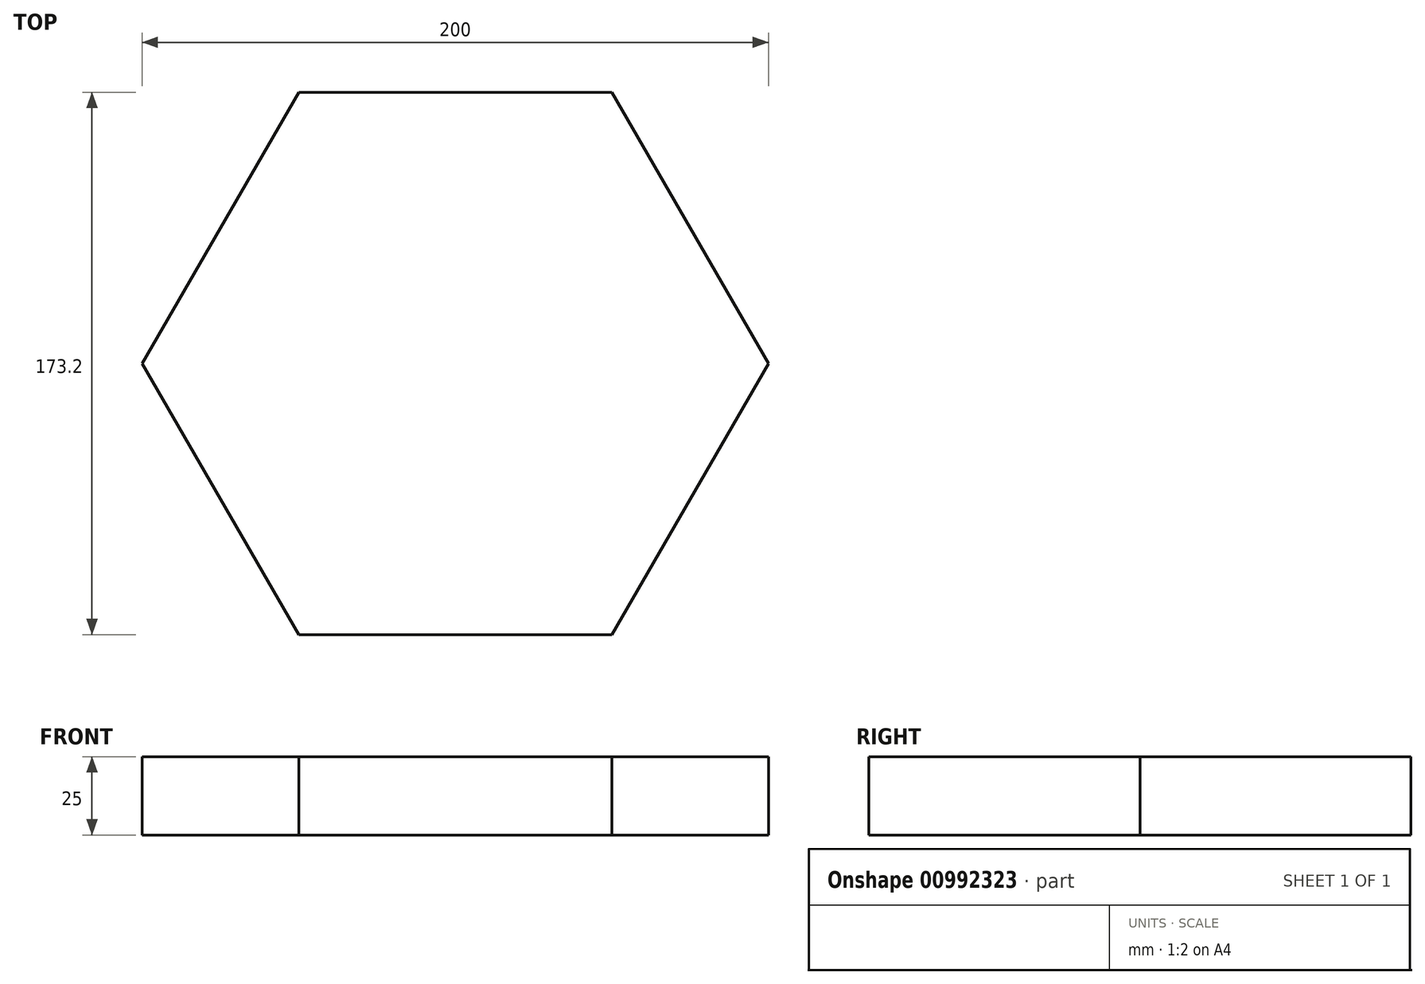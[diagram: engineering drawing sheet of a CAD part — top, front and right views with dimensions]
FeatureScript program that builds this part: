
annotation { "Feature Type Name" : "Feature", "Feature Type Description" : "" }
export const myFeature = defineFeature(function(context is Context, id is Id, definition is map)
    precondition{}
    {
        {
            var Q0;
            Q0=qCreatedBy(makeId("Top.planeOp"),FACE);
            var sketch = newSketch(context, id + "F0", { "sketchPlane" : qUnion([Q0])});
            skCircle(sketch, "E0", {"center": v(0, 0) * mm, "radius": 100 * mm});
            skLineSegment(sketch, "E1", {"start": v(0, 0) * mm, "end": v(100, 0) * mm, "construction": true});
            skLineSegment(sketch, "E2", {"start": v(0, 0) * mm, "end": v(50, 86.6) * mm, "construction": true});
            skLineSegment(sketch, "E3", {"start": v(0, 0) * mm, "end": v(-50, 86.6) * mm, "construction": true});
            skLineSegment(sketch, "E4", {"start": v(0, 0) * mm, "end": v(-100, 0) * mm, "construction": true});
            skLineSegment(sketch, "E5", {"start": v(0, 0) * mm, "end": v(-50, -86.6) * mm, "construction": true});
            skLineSegment(sketch, "E6", {"start": v(0, 0) * mm, "end": v(50, -86.6) * mm, "construction": true});
            skLineSegment(sketch, "E7", {"start": v(-50, 86.6) * mm, "end": v(50, 86.6) * mm});
            skLineSegment(sketch, "E8", {"start": v(50, 86.6) * mm, "end": v(100, 0) * mm});
            skLineSegment(sketch, "E9", {"start": v(100, 0) * mm, "end": v(50, -86.6) * mm});
            skLineSegment(sketch, "E10", {"start": v(50, -86.6) * mm, "end": v(-50, -86.6) * mm});
            skLineSegment(sketch, "E11", {"start": v(-50, -86.6) * mm, "end": v(-100, 0) * mm});
            skLineSegment(sketch, "E12", {"start": v(-100, 0) * mm, "end": v(-50, 86.6) * mm});
            skSolve(sketch);
        }
        {
            var Q0;
            Q0=sQuery(id+"F0.wireOp",EDGE,"E7");
            var Q1;
            Q1=sQuery(id+"F0.wireOp",EDGE,"E8");
            var Q2;
            Q2=sQuery(id+"F0.wireOp",EDGE,"E9");
            var Q3;
            Q3=sQuery(id+"F0.wireOp",EDGE,"E10");
            var Q4;
            Q4=sQuery(id+"F0.wireOp",EDGE,"E11");
            var Q5;
            Q5=sQuery(id+"F0.wireOp",EDGE,"E12");
            extrude(context, id + "F1", {"bodyType" : ToolBodyType.SURFACE, "surfaceEntities" : qUnion([Q0, Q1, Q2, Q3, Q4, Q5]), "depth" : 25 * mm, "offsetDistance" : 25 * mm});
        }
    });
